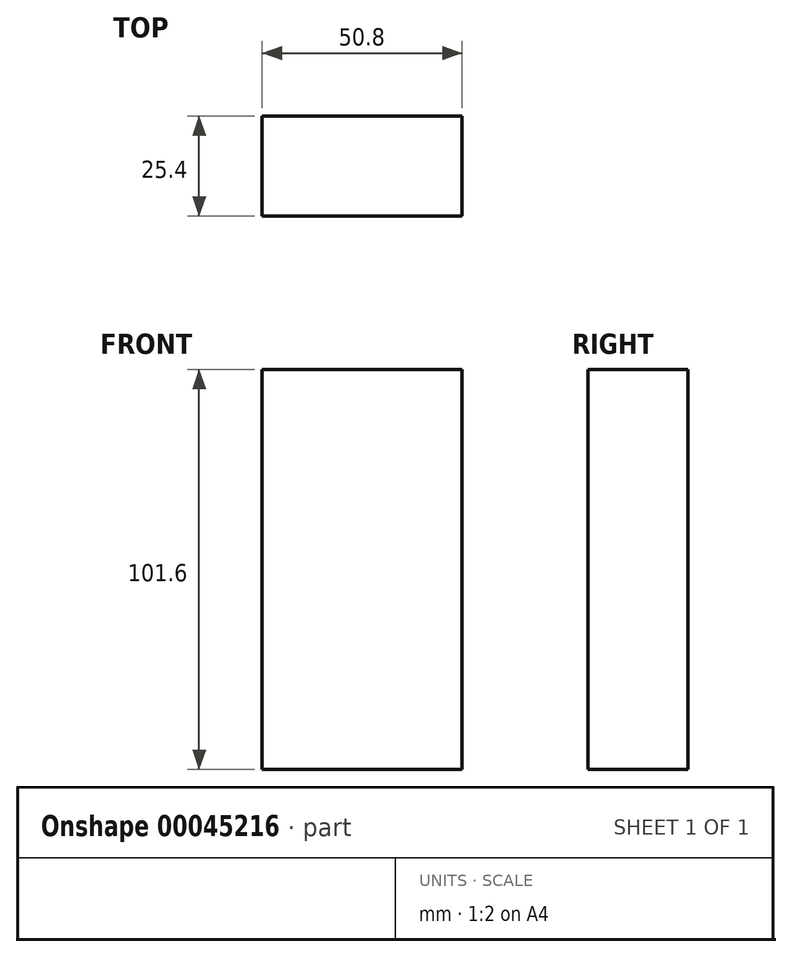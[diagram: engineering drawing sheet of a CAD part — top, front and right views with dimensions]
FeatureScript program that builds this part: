
annotation { "Feature Type Name" : "Feature", "Feature Type Description" : "" }
export const myFeature = defineFeature(function(context is Context, id is Id, definition is map)
    precondition{}
    {
        {
            var Q0;
            Q0=qCreatedBy(makeId("Front.planeOp"),FACE);
            var sketch = newSketch(context, id + "F0", { "sketchPlane" : qUnion([Q0])});
            skLineSegment(sketch, "E0.rect.bottom", {"start": v(25.4, -50.8) * mm, "end": v(-25.4, -50.8) * mm});
            skLineSegment(sketch, "E0.rect.top", {"start": v(25.4, 50.8) * mm, "end": v(-25.4, 50.8) * mm});
            skLineSegment(sketch, "E0.rect.left", {"start": v(25.4, -50.8) * mm, "end": v(25.4, 50.8) * mm});
            skLineSegment(sketch, "E0.rect.right", {"start": v(-25.4, -50.8) * mm, "end": v(-25.4, 50.8) * mm});
            skPoint(sketch, "E0.rect.middle", {"position": v(0, 0) * mm});
            skSolve(sketch);
        }
        {
            var Q0;
            Q0=makeQuery(id+"F0.imprint","IMPRINT",FACE,{"disambiguationData":[TD([[makeQuery(id+"F0.imprint","IMPRINT",EDGE,{"derivedFrom":sQuery(id+"F0.wireOp",EDGE,"E0.rect.bottom")}),-1.0]])]});
            extrude(context, id + "F1", {"entities" : qUnion([Q0]), "depth" : 25.4 * mm});
        }
    });
